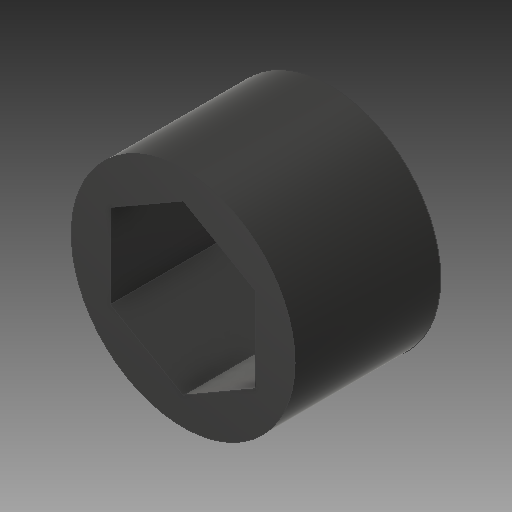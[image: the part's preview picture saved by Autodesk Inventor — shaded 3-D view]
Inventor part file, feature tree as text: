
AUTODESK INVENTOR PART (.ipt)
format: ipt  version: 2017 (Build 210142000, 142)  size: 107,520 bytes
history: native  units: in
note: dims shown in document units (in); Inventor stores cm internally (conversion verified against a paired STEP export)
features: extrude x1, sketch x1
ambient origin geometry x8: Origin, YZ Plane, XZ Plane, XY Plane, X Axis, Y Axis, Z Axis, Center Point
bodies: Solid1 (feature_tree)
feature tree (2):
  extrude  "Extrusion1"  Depth=0.5in
  sketch  "Sketch1"  dims[d0=0.5in d1=0.768in d2=0.5in d3=0.0in]
